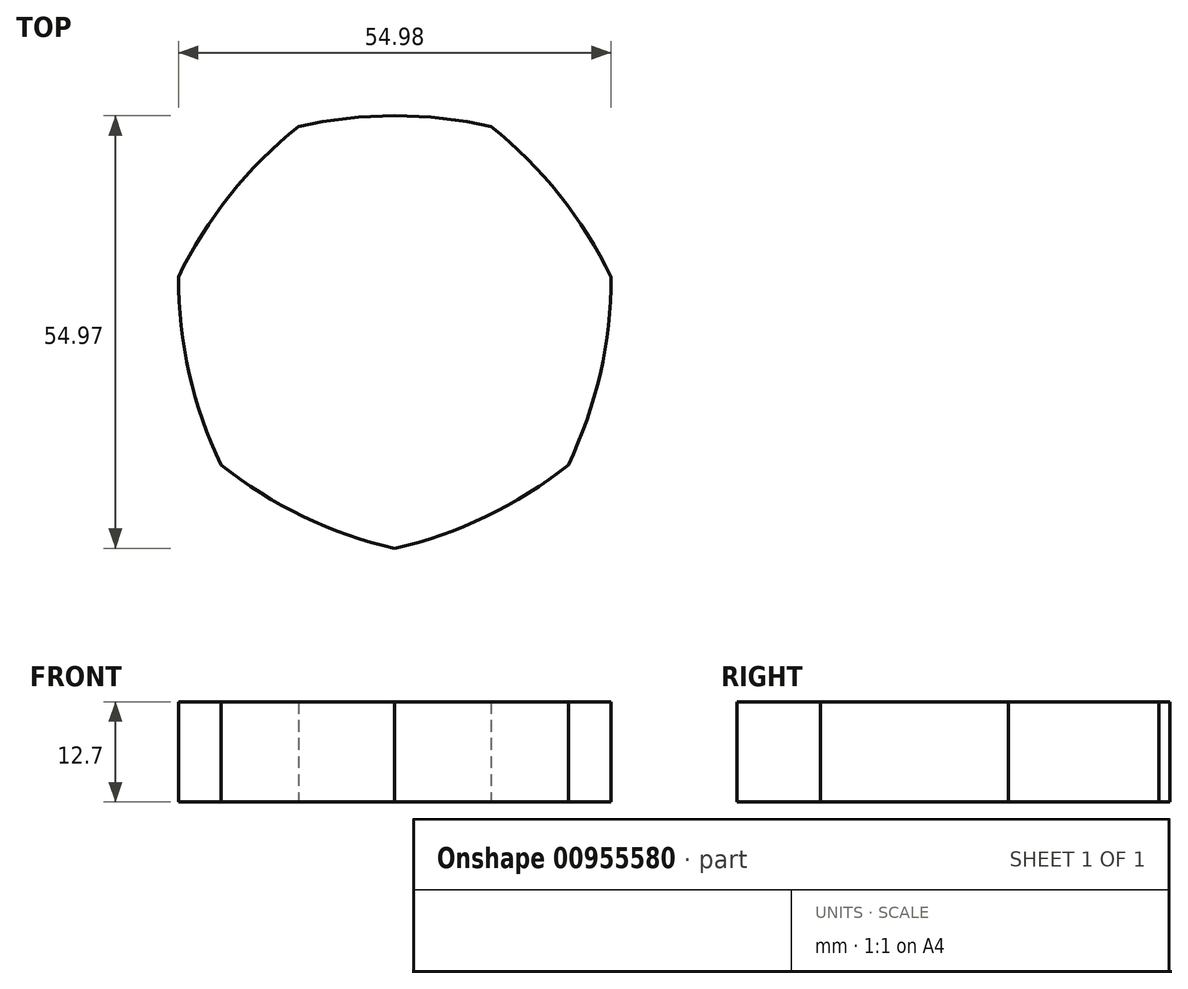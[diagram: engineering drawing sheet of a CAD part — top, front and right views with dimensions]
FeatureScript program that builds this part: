
annotation { "Feature Type Name" : "Feature", "Feature Type Description" : "" }
export const myFeature = defineFeature(function(context is Context, id is Id, definition is map)
    precondition{}
    {
        {
            var Q0;
            Q0=qCreatedBy(makeId("Top.planeOp"),FACE);
            var sketch = newSketch(context, id + "F0", { "sketchPlane" : qUnion([Q0])});
            skCircle(sketch, "E0.cCircle", {"center": v(0, 0) * mm, "radius": 25.4 * mm, "construction": true});
            skLineSegment(sketch, "E0.0", {"start": v(-12.23, 25.4) * mm, "end": v(12.23, 25.4) * mm, "construction": true});
            skLineSegment(sketch, "E0.1", {"start": v(12.23, 25.4) * mm, "end": v(27.49, 6.27) * mm, "construction": true});
            skLineSegment(sketch, "E0.2", {"start": v(27.49, 6.27) * mm, "end": v(22.04, -17.58) * mm, "construction": true});
            skLineSegment(sketch, "E0.3", {"start": v(22.04, -17.58) * mm, "end": v(0, -28.2) * mm, "construction": true});
            skLineSegment(sketch, "E0.4", {"start": v(0, -28.2) * mm, "end": v(-22.04, -17.58) * mm, "construction": true});
            skLineSegment(sketch, "E0.5", {"start": v(-22.04, -17.58) * mm, "end": v(-27.49, 6.27) * mm, "construction": true});
            skLineSegment(sketch, "E0.6", {"start": v(-27.49, 6.27) * mm, "end": v(-12.23, 25.4) * mm, "construction": true});
            skPoint(sketch, "E0.0.midPoint", {"position": v(0, 25.4) * mm});
            skArc(sketch, "E1", {"start": v(12.23, 25.4) * mm, "mid": v(0, 26.78) * mm, "end": v(-12.23, 25.4) * mm});
            skArc(sketch, "E2", {"start": v(27.49, 6.27) * mm, "mid": v(20.94, 16.7) * mm, "end": v(12.23, 25.4) * mm});
            skArc(sketch, "E3", {"start": v(22.04, -17.58) * mm, "mid": v(26.1, -5.96) * mm, "end": v(27.49, 6.27) * mm});
            skArc(sketch, "E4", {"start": v(0, -28.2) * mm, "mid": v(11.62, -24.13) * mm, "end": v(22.04, -17.58) * mm});
            skArc(sketch, "E5", {"start": v(-22.04, -17.58) * mm, "mid": v(-11.62, -24.13) * mm, "end": v(0, -28.2) * mm});
            skArc(sketch, "E6", {"start": v(-27.49, 6.27) * mm, "mid": v(-26.1, -5.96) * mm, "end": v(-22.04, -17.58) * mm});
            skArc(sketch, "E7", {"start": v(-12.23, 25.4) * mm, "mid": v(-20.94, 16.7) * mm, "end": v(-27.49, 6.27) * mm});
            skSolve(sketch);
        }
        {
            var Q0;
            Q0=makeQuery(id+"F0.imprint","IMPRINT",FACE,{"disambiguationData":[TD([[makeQuery(id+"F0.imprint","IMPRINT",EDGE,{"derivedFrom":sQuery(id+"F0.wireOp",EDGE,"E1")}),1.0]])]});
            extrude(context, id + "F1", {"entities" : qUnion([Q0]), "depth" : 12.7 * mm, "offsetDistance" : 25.4 * mm});
        }
    });
